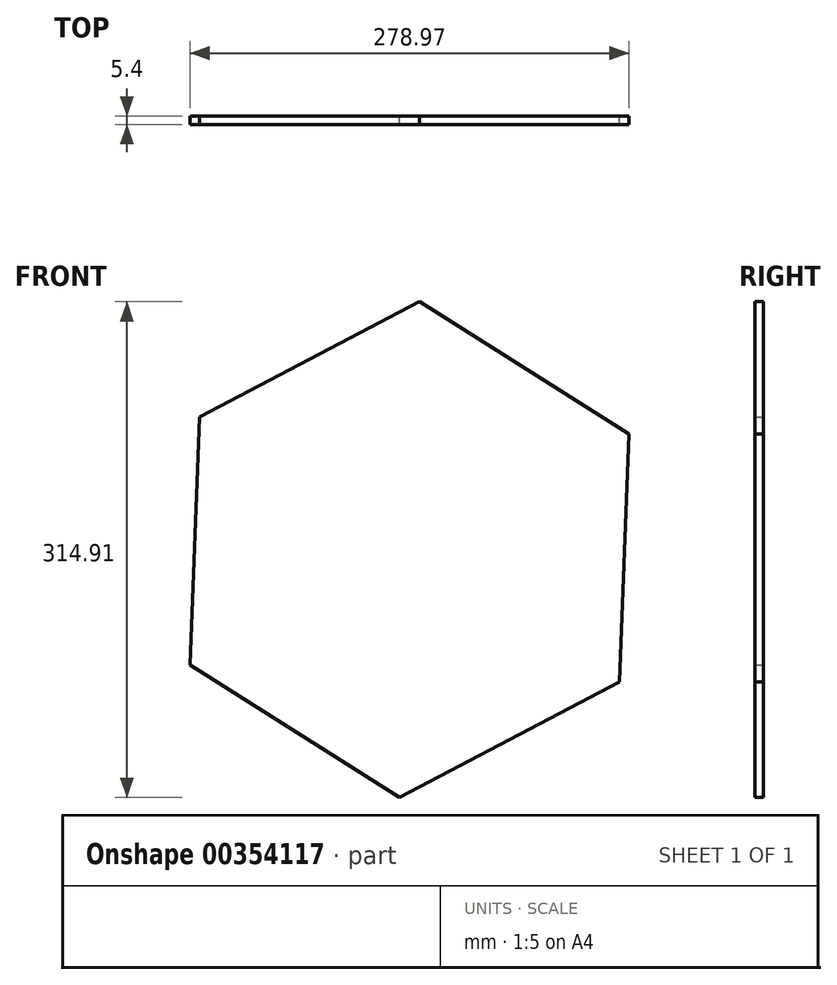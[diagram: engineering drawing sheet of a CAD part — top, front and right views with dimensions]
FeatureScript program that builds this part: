
annotation { "Feature Type Name" : "Feature", "Feature Type Description" : "" }
export const myFeature = defineFeature(function(context is Context, id is Id, definition is map)
    precondition{}
    {
        {
            var Q0;
            Q0=qCreatedBy(makeId("Front.planeOp"),FACE);
            var sketch = newSketch(context, id + "F0", { "sketchPlane" : qUnion([Q0])});
            skCircle(sketch, "E0.cCircle", {"center": v(84.96, 31.37) * mm, "radius": 157.58 * mm, "construction": true});
            skLineSegment(sketch, "E0.0", {"start": v(-54.53, -41.95) * mm, "end": v(-48.28, 115.51) * mm});
            skLineSegment(sketch, "E0.1", {"start": v(-48.28, 115.51) * mm, "end": v(91.21, 188.82) * mm});
            skLineSegment(sketch, "E0.2", {"start": v(91.21, 188.82) * mm, "end": v(224.44, 104.68) * mm});
            skLineSegment(sketch, "E0.3", {"start": v(224.44, 104.68) * mm, "end": v(218.19, -52.78) * mm});
            skLineSegment(sketch, "E0.4", {"start": v(218.19, -52.78) * mm, "end": v(78.7, -126.1) * mm});
            skLineSegment(sketch, "E0.5", {"start": v(78.7, -126.1) * mm, "end": v(-54.53, -41.95) * mm});
            skSolve(sketch);
        }
        {
            var Q0;
            Q0 = qSketchRegion(id + "F0", true);
            var Q1;
            Q1=makeQuery(id+"F0.imprint","IMPRINT",FACE,{"disambiguationData":[TD([[makeQuery(id+"F0.imprint","IMPRINT",EDGE,{"derivedFrom":sQuery(id+"F0.wireOp",EDGE,"E0.0")}),-1.0]])]});
            extrude(context, id + "F1", {"entities" : qUnion([Q0, Q1]), "depth" : 5.4 * mm});
        }
    });
